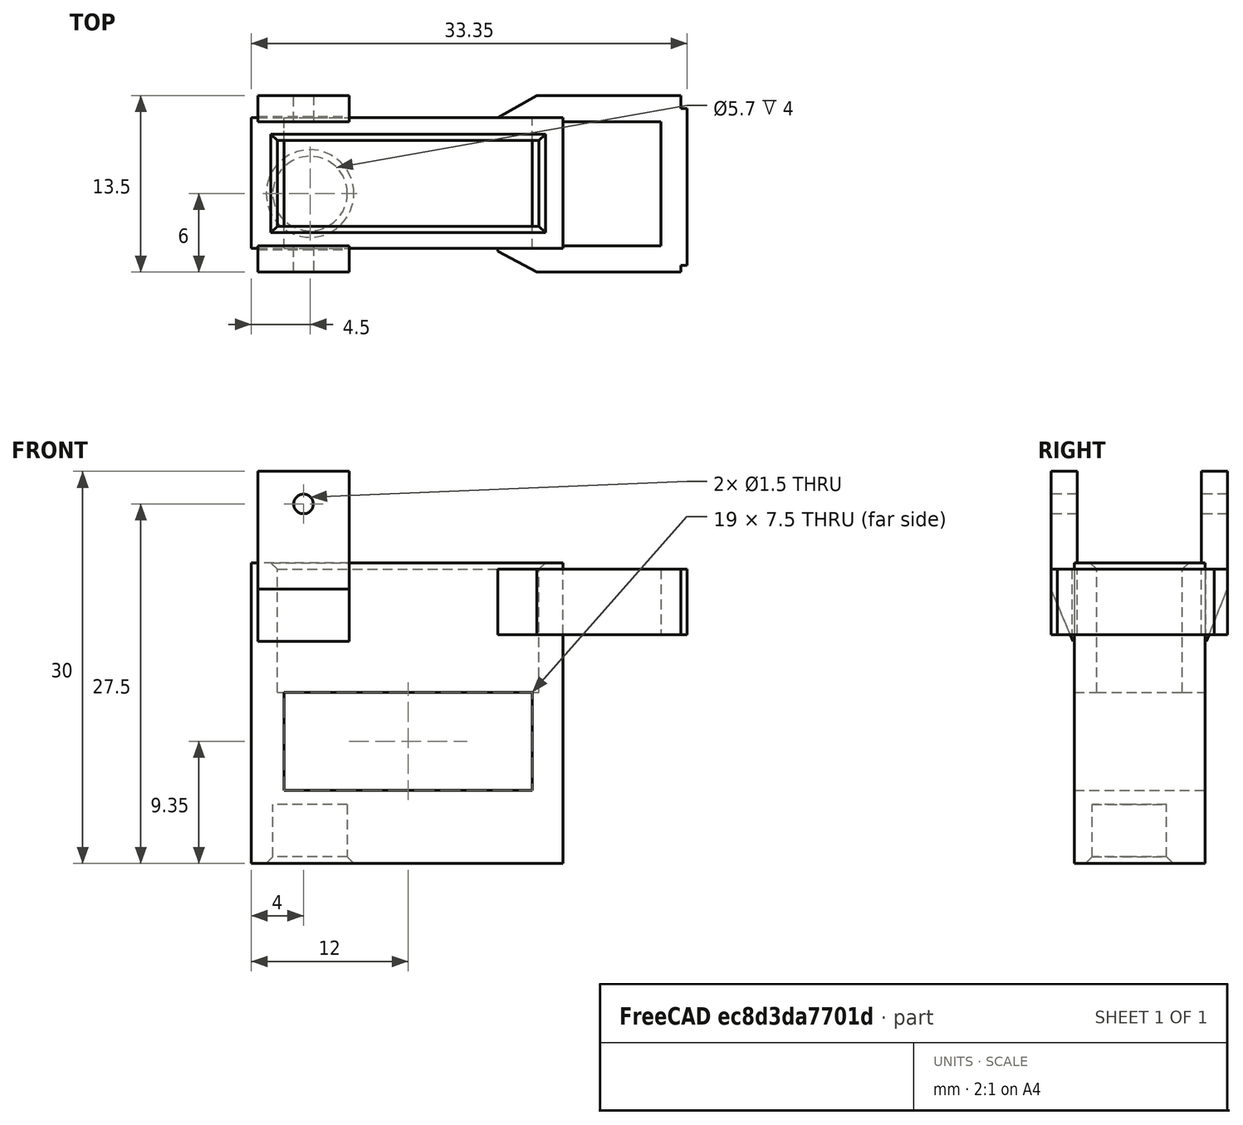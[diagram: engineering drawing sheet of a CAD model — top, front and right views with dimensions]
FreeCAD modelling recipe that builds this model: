
FCSTD DOCUMENT  (FreeCAD 1.0R39285 (Git))
Label: holder
License: All rights reserved
LicenseURL: https://en.wikipedia.org/wiki/All_rights_reserved
objects: PartDesign::AdditiveBox×6, PartDesign::Chamfer×6, PartDesign::SubtractiveBox×2, PartDesign::SubtractiveCylinder×2, PartDesign::Body×1
note: 49 computed .brp shape members not serialized (recipe doc carries the construction recipe); baked Part::Feature solids carry a one-line shape summary decoded from their .brp

FEATURE [PartDesign::AdditiveBox] Box
  AttacherType = Attacher::AttachEngine3D
  Height = 23
  Length = 23.85
  Refine = true
  Suppressed = false
  Width = 10
FEATURE [PartDesign::SubtractiveBox] Box001
  AttacherType = Attacher::AttachEngine3D
  AttachmentOffset = pos=(2,1.7,-9.9) rot=(0,0,1;0rad)
  AttachmentSupport = -> [Box]
  BaseFeature = -> Box
  Height = 9.9
  Length = 20
  MapMode = 5
  Placement = pos=(2,1.7,13.1) rot=(0,0,1;0rad)
  Refine = true
  Suppressed = false
  Width = 6.55
FEATURE [PartDesign::SubtractiveBox] Box002
  AttacherType = Attacher::AttachEngine3D
  AttachmentOffset = pos=(0.5,-4.5,-7.5) rot=(0,0,1;0rad)
  AttachmentSupport = -> [Box001]
  BaseFeature = -> Box001
  Height = 7.5
  Length = 19
  MapMode = 5
  Placement = pos=(2.5,-2.8,5.6) rot=(0,0,1;0rad)
  Refine = true
  Suppressed = false
  Width = 15
FEATURE [PartDesign::Chamfer] Chamfer
  Angle = 45
  Base = -> Box002 [Edge16,Edge15,Edge14,Edge17]
  BaseFeature = -> Box002
  ChamferType = 0
  FlipDirection = false
  Placement = pos=(2.5,-2.8,5.6) rot=(0,0,1;0rad)
  Refine = true
  Size = 0.5
  Size2 = 1
  SupportTransform = false
  Suppressed = false
  UseAllEdges = false
FEATURE [PartDesign::SubtractiveCylinder] Cylinder
  Angle = 360
  AttacherType = Attacher::AttachEngine3D
  AttachmentOffset = pos=(2,-7,-4.5) rot=(0,0,1;0rad)
  AttachmentSupport = -> [Chamfer]
  BaseFeature = -> Chamfer
  FirstAngle = 0
  Height = 4.5
  MapMode = 5
  Placement = pos=(4.5,4.2,4.5) rot=(1,0,0;3.14159rad)
  Radius = 2.85
  Refine = true
  SecondAngle = 0
  Suppressed = false
FEATURE [PartDesign::Chamfer] Chamfer001
  Angle = 45
  Base = -> Cylinder [Edge45]
  BaseFeature = -> Cylinder
  ChamferType = 0
  FlipDirection = false
  Placement = pos=(4.5,4.2,4.5) rot=(1,0,0;3.14159rad)
  Refine = true
  Size = 0.5
  Size2 = 1
  SupportTransform = false
  Suppressed = false
  UseAllEdges = false
FEATURE [PartDesign::AdditiveBox] Box003
  AttacherType = Attacher::AttachEngine3D
  AttachmentOffset = pos=(-4,-6,-6) rot=(0,0,1;0rad)
  AttachmentSupport = -> [Chamfer001]
  BaseFeature = -> Chamfer001
  Height = 13
  Length = 7
  MapMode = 5
  Placement = pos=(0.5,-1.8,17) rot=(0,0,1;0rad)
  Refine = true
  Suppressed = false
  Width = 2
FEATURE [PartDesign::Chamfer] Chamfer002
  Angle = 45
  Base = -> Box003 [Edge51]
  BaseFeature = -> Box003
  ChamferType = 1
  FlipDirection = false
  Placement = pos=(0.5,-1.8,17) rot=(0,0,1;0rad)
  Refine = true
  Size = 1.7
  Size2 = 4
  SupportTransform = false
  Suppressed = false
  UseAllEdges = false
FEATURE [PartDesign::AdditiveBox] Box004
  AttacherType = Attacher::AttachEngine3D
  AttachmentOffset = pos=(0,11.5,0) rot=(0,0,1;0rad)
  AttachmentSupport = -> [Chamfer002]
  BaseFeature = -> Chamfer002
  Height = 13
  Length = 7
  MapMode = 2
  Placement = pos=(0.5,9.7,17) rot=(0,0,1;0rad)
  Refine = true
  Suppressed = false
  Width = 2
  expr: Height = 13 mm
FEATURE [PartDesign::SubtractiveCylinder] Cylinder001
  Angle = 360
  AttacherType = Attacher::AttachEngine3D
  AttachmentOffset = pos=(-3.5,10.5,-3) rot=(0,0,1;0rad)
  AttachmentSupport = -> [Box004]
  BaseFeature = -> Box004
  FirstAngle = 0
  Height = 15
  MapMode = 5
  Placement = pos=(4,-2.8,27.5) rot=(0,0.707107,0.707107;3.14159rad)
  Radius = 0.75
  Refine = true
  SecondAngle = 0
  Suppressed = false
FEATURE [PartDesign::Chamfer] Chamfer003
  Angle = 45
  Base = -> Cylinder001 [Edge95]
  BaseFeature = -> Cylinder001
  ChamferType = 1
  FlipDirection = false
  Placement = pos=(4,-2.8,27.5) rot=(0,0.707107,0.707107;3.14159rad)
  Refine = true
  Size = 1.6
  Size2 = 4
  SupportTransform = false
  Suppressed = false
  UseAllEdges = false
FEATURE [PartDesign::AdditiveBox] Box005
  AttacherType = Attacher::AttachEngine3D
  AttachmentOffset = pos=(5,1,-5) rot=(0,0,1;0rad)
  AttachmentSupport = -> [Chamfer003]
  BaseFeature = -> Chamfer003
  Height = 14
  Length = 5
  MapMode = 5
  Placement = pos=(18.85,-1.8,22.5) rot=(0,1,0;1.5708rad)
  Refine = true
  Suppressed = false
  Width = 2
FEATURE [PartDesign::Chamfer] Chamfer004
  Angle = 45
  Base = -> Box005 [Edge113]
  BaseFeature = -> Box005
  ChamferType = 1
  FlipDirection = false
  Placement = pos=(18.85,-1.8,22.5) rot=(0,1,0;1.5708rad)
  Refine = true
  Size = 1.6
  Size2 = 3
  SupportTransform = false
  Suppressed = false
  UseAllEdges = false
FEATURE [PartDesign::AdditiveBox] Box006
  AttacherType = Attacher::AttachEngine3D
  AttachmentOffset = pos=(0,11.5,0) rot=(0,0,1;0rad)
  AttachmentSupport = -> [Chamfer004]
  BaseFeature = -> Chamfer004
  Height = 14
  Length = 5
  MapMode = 2
  Placement = pos=(18.85,9.7,22.5) rot=(0,1,0;1.5708rad)
  Refine = true
  Suppressed = false
  Width = 2
FEATURE [PartDesign::Chamfer] Chamfer005
  Angle = 45
  Base = -> Box006 [Edge133]
  BaseFeature = -> Box006
  ChamferType = 1
  FlipDirection = false
  Placement = pos=(18.85,9.7,22.5) rot=(0,1,0;1.5708rad)
  Refine = true
  Size = 1.69
  Size2 = 3
  SupportTransform = false
  Suppressed = false
  UseAllEdges = false
FEATURE [PartDesign::AdditiveBox] Box007
  AttacherType = Attacher::AttachEngine3D
  AttachmentOffset = pos=(0,-11,-1.5) rot=(0,0,1;0rad)
  AttachmentSupport = -> [Chamfer005]
  BaseFeature = -> Chamfer005
  Height = 2
  Length = 5
  MapMode = 5
  Placement = pos=(31.35,-1.3,22.5) rot=(0,1,0;1.5708rad)
  Refine = true
  Suppressed = false
  Width = 12
FEATURE [PartDesign::Body] Body
  AllowCompound = false
  Group = -> [Box,Box001,Box002,Chamfer,Cylinder,Chamfer001,Box003,Chamfer002,Box004,Cylinder001,Chamfer003,Box005,Chamfer004,Box006,Chamfer005,Box007]
  Origin = -> Origin
  Tip = -> Box007
